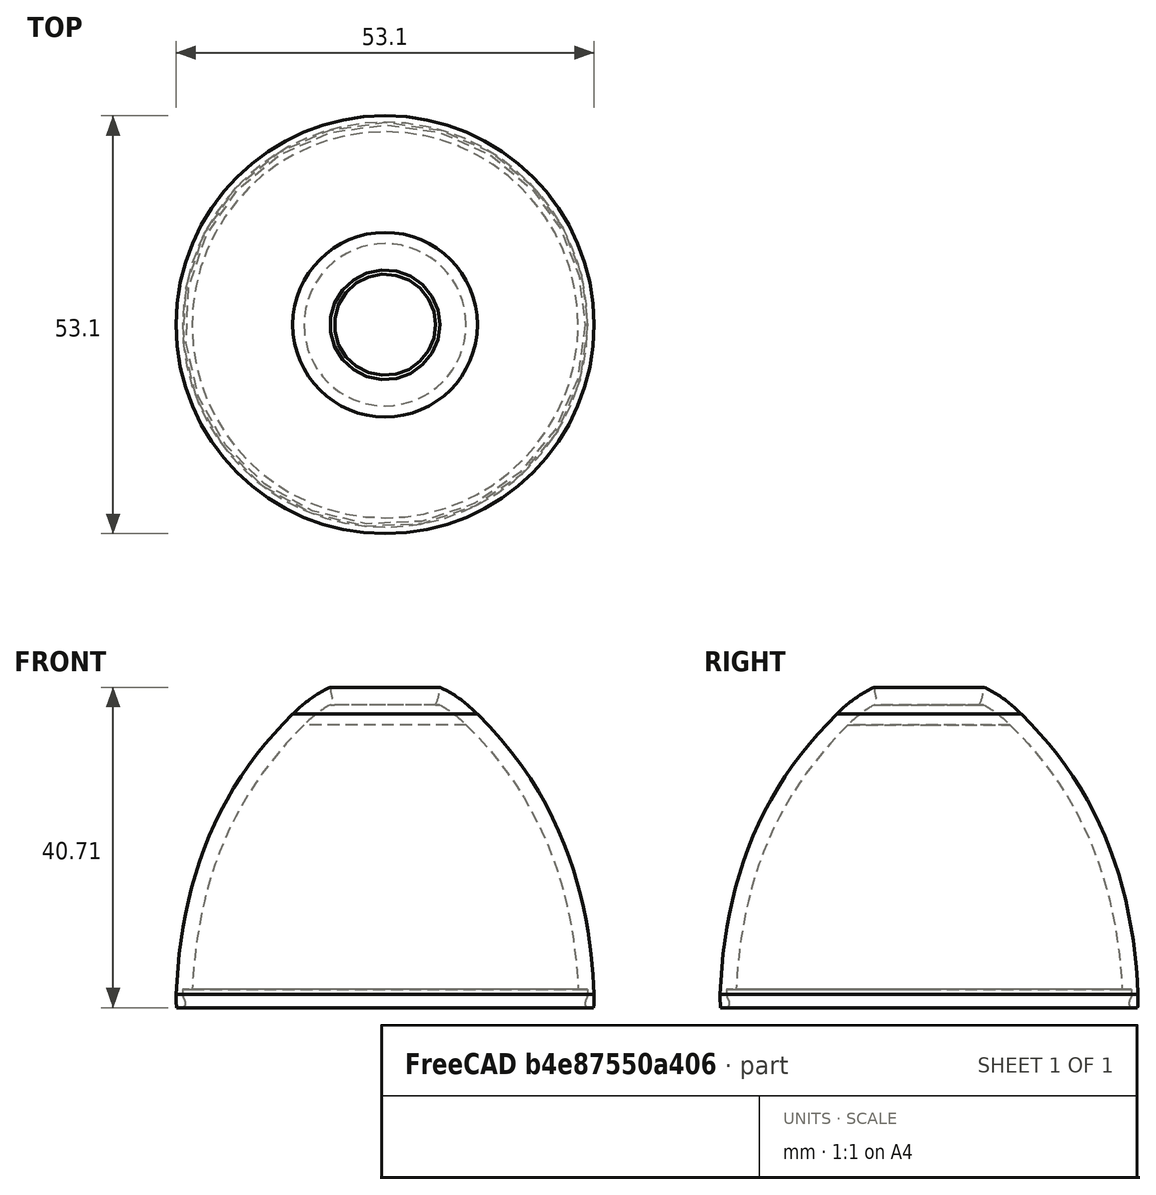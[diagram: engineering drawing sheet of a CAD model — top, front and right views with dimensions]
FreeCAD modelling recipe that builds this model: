
FCSTD DOCUMENT  (FreeCAD 0.19R22284 (Git))
Label: enclosure_freecad
License: All rights reserved
LicenseURL: http://en.wikipedia.org/wiki/All_rights_reserved
objects: Part::Feature×8, Part::Revolution×2, Part::Cut×2, Part::Sphere×1, Part::Extrusion×1
note: 14 computed .brp shape members not serialized (recipe doc carries the construction recipe); baked Part::Feature solids carry a one-line shape summary decoded from their .brp

FEATURE [Part::Feature] path4245
  Placement = pos=(-25,25,85) rot=(1,0,0;1.5708rad)
  shape: bbox 26.48 x 2e-07 x 27.14 mm, 0 faces, 0 solids (baked)
FEATURE [Part::Feature] path4237
  Placement = pos=(20,-25,60) rot=(1,0,0;1.5708rad)
  shape: bbox 26.55 x 2e-07 x 42.29 mm, 0 faces, 0 solids (baked)
FEATURE [Part::Feature] rect3630
  Placement = pos=(-38.2549,43.89,0) rot=(0,0,1;0rad)
  shape: bbox 17 x 1.5 x 2e-07 mm, 1 faces, 0 solids (baked)
FEATURE [Part::Feature] path4279
  Placement = pos=(167,55,38.67) rot=(0,0,1;0rad)
  shape: bbox 12.8 x 12.8 x 2e-07 mm, 1 faces, 0 solids (baked)
FEATURE [Part::Revolution] Revolve
  Angle = 360
  Axis = (0,0,1)
  Base = (-25,25,85)
  FaceMakerClass = Part::FaceMakerBullseye
  Solid = false
  Source = -> path4245
  Symmetric = false
FEATURE [Part::Revolution] Revolve001
  Angle = 360
  Axis = (0,0,1)
  Base = (20,-25,60)
  FaceMakerClass = Part::FaceMakerBullseye
  Placement = pos=(0.0595158,0.126283,0) rot=(0,0,1;0rad)
  Solid = false
  Source = -> path4237
  Symmetric = false
FEATURE [Part::Sphere] Sphere
  Angle1 = -90
  Angle2 = 90
  Angle3 = 360
  AttacherType = Attacher::AttachEngine3D
  Placement = pos=(20.0595,-24.8737,41.45) rot=(0,-1,0;0.763388rad)
  Radius = 7
FEATURE [Part::Feature] Revolve001_solid  label="Revolve001 (Solid)"
  shape: bbox 53.1 x 53.1 x 42.29 mm, 11 faces (baked)
FEATURE [Part::Cut] Cut
  Base = -> Revolve001_solid
  Tool = -> Sphere
FEATURE [Part::Feature] Revolve_solid  label="Revolve (Solid)"
  shape: bbox 52.96 x 52.96 x 27.14 mm, 8 faces (baked)
FEATURE [Part::Extrusion] Extrude
  Base = -> rect3630
  Dir = (0,0,5)
  DirMode = 0
  FaceMakerClass = Part::FaceMakerBullseye
  LengthFwd = 10
  LengthRev = 0
  Solid = false
  Symmetric = false
FEATURE [Part::Cut] Cut001
  Base = -> Revolve_solid
  Tool = -> Extrude
FEATURE [Part::Feature] Cut001_solid  label="Cut001 (Solid)"
  shape: bbox 52.96 x 52.96 x 27.14 mm, 12 faces (baked)
FEATURE [Part::Feature] Cut_solid  label="Cut (Solid)"
  shape: bbox 53.1 x 53.1 x 48.21 mm, 12 faces (baked)
